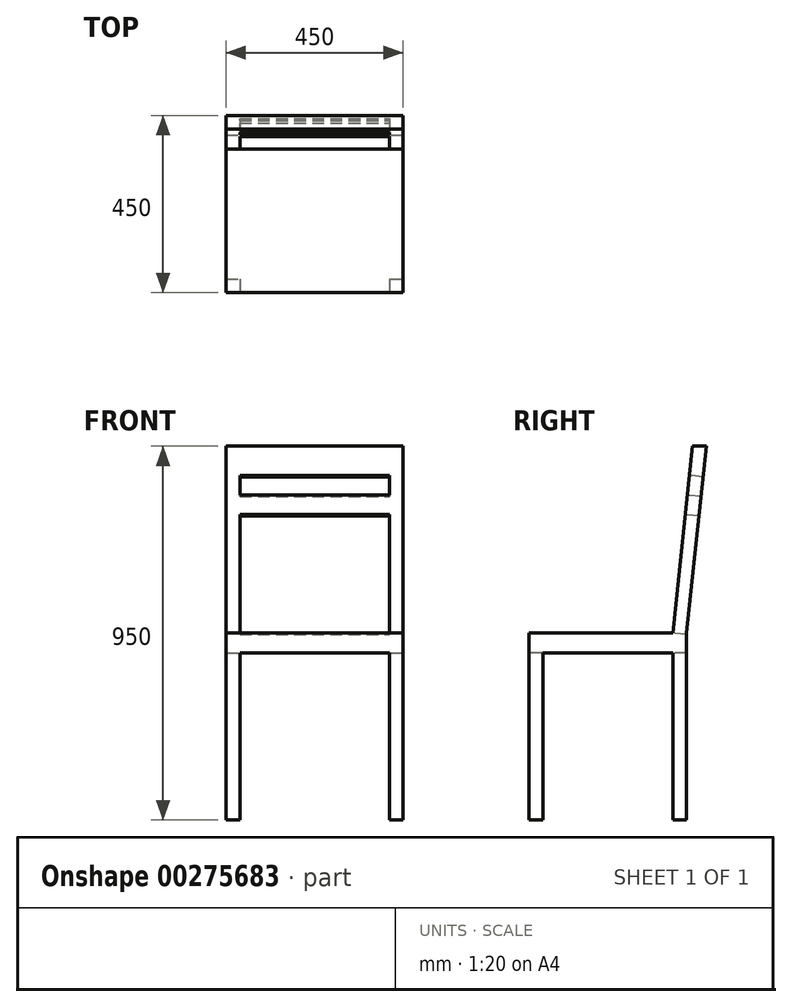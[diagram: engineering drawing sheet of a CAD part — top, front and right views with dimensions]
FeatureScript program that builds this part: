
annotation { "Feature Type Name" : "Feature", "Feature Type Description" : "" }
export const myFeature = defineFeature(function(context is Context, id is Id, definition is map)
    precondition{}
    {
        {
            var Q0;
            Q0=qCreatedBy(makeId("Top.planeOp"),FACE);
            var sketch = newSketch(context, id + "F0", { "sketchPlane" : qUnion([Q0])});
            skLineSegment(sketch, "E0.bottom", {"start": v(225, 225) * mm, "end": v(-225, 225) * mm});
            skLineSegment(sketch, "E0.top", {"start": v(225, -225) * mm, "end": v(-225, -225) * mm});
            skLineSegment(sketch, "E0.left", {"start": v(225, 225) * mm, "end": v(225, -225) * mm});
            skLineSegment(sketch, "E0.right", {"start": v(-225, 225) * mm, "end": v(-225, -225) * mm});
            skPoint(sketch, "E0.middle", {"position": v(0, 0) * mm});
            skSolve(sketch);
        }
        {
            var Q0;
            Q0=qSketchRegion(id+"F0",true);
            extrude(context, id + "F1", {"entities" : qUnion([Q0]), "depth" : 950 * mm});
        }
        {
            var Q0;
            Q0=makeQuery(id+"F1.opExtrude","SWEPT_FACE",FACE,{"disambiguationData":[OSD([sQuery(id+"F0.wireOp",EDGE,"E0.left")])]});
            var sketch = newSketch(context, id + "F2", { "sketchPlane" : qUnion([Q0])});
            skLineSegment(sketch, "E1.bottom", {"start": v(225, 475) * mm, "end": v(-225, 475) * mm});
            skLineSegment(sketch, "E1.top", {"start": v(225, 475) * mm, "end": v(-225, 475) * mm});
            skLineSegment(sketch, "E1.left", {"start": v(225, 475) * mm, "end": v(225, 475) * mm});
            skLineSegment(sketch, "E1.right", {"start": v(-225, 475) * mm, "end": v(-225, 475) * mm});
            skLineSegment(sketch, "E2.bottom", {"start": v(-225, 425) * mm, "end": v(225, 425) * mm});
            skLineSegment(sketch, "E2.top", {"start": v(-225, 475) * mm, "end": v(225, 475) * mm});
            skLineSegment(sketch, "E2.left", {"start": v(-225, 425) * mm, "end": v(-225, 475) * mm});
            skLineSegment(sketch, "E2.right", {"start": v(225, 425) * mm, "end": v(225, 475) * mm});
            skLineSegment(sketch, "E3", {"start": v(225, 950) * mm, "end": v(175, 475) * mm});
            skLineSegment(sketch, "E4", {"start": v(190, 950) * mm, "end": v(140, 475) * mm});
            skLineSegment(sketch, "E5", {"start": v(140, 475) * mm, "end": v(140, 0) * mm});
            skLineSegment(sketch, "E6", {"start": v(175, 475) * mm, "end": v(175, 0) * mm});
            skLineSegment(sketch, "E7.bottom", {"start": v(-225, 425) * mm, "end": v(-190, 425) * mm});
            skLineSegment(sketch, "E7.top", {"start": v(-225, 0) * mm, "end": v(-190, 0) * mm});
            skLineSegment(sketch, "E7.left", {"start": v(-225, 425) * mm, "end": v(-225, 0) * mm});
            skLineSegment(sketch, "E7.right", {"start": v(-190, 425) * mm, "end": v(-190, 0) * mm});
            skSolve(sketch);
        }
        {
            var Q0;
            {var subQ0=sQuery(id+"F2.wireOp",EDGE,"E2.right");Q0=makeQuery(id+"F2.imprint","IMPRINT",FACE,{"disambiguationData":[TD([[makeQuery(id+"F2.imprint","IMPRINT",EDGE,{"derivedFrom":subQ0}),-1.0]])]});}
            var Q1;
            {var subQ4=sQuery(id+"F2.wireOp",EDGE,"E4");Q1=makeQuery(id+"F2.imprint","IMPRINT",FACE,{"disambiguationData":[TD([[makeQuery(id+"F2.imprint","IMPRINT",EDGE,{"derivedFrom":subQ4}),-1.0]])]});}
            var Q2;
            {var subQ0=sQuery(id+"F2.wireOp",EDGE,"E7.right");Q2=makeQuery(id+"F2.imprint","IMPRINT",FACE,{"disambiguationData":[TD([[makeQuery(id+"F2.imprint","IMPRINT",EDGE,{"derivedFrom":subQ0}),1.0]])]});}
            var Q3;
            {var subQ1=sQuery(id+"F0.wireOp",EDGE,"E0.left");var subQ4=sQuery(id+"F2.wireOp",EDGE,"E6");var subQ6=makeQuery(id+"F1.opExtrude","CAP_EDGE",EDGE,{"disambiguationData":[OSD([subQ1])],"isStart":true});var subQ7=makeQuery(id+"F2.imprint","INTERSECT",VERTEX,{"derivedFrom":[subQ6,subQ4]});Q3=makeQuery(id+"F2.imprint","IMPRINT",FACE,{"disambiguationData":[TD([[makeQuery(id+"F2.imprint","IMPRINT",EDGE,{"disambiguationData":[TD([[subQ7,1.0]])],"derivedFrom":subQ4}),1.0]])]});}
            var Q4;
            {var subQ4=sQuery(id+"F2.wireOp",EDGE,"E3");Q4=makeQuery(id+"F2.imprint","IMPRINT",FACE,{"disambiguationData":[TD([[makeQuery(id+"F2.imprint","IMPRINT",EDGE,{"derivedFrom":subQ4}),1.0]])]});}
            extrude(context, id + "F3", {"entities" : qUnion([Q0, Q1, Q2, Q3, Q4]), "operationType" : NewBodyOperationType.REMOVE, "endBound" : BoundingType.THROUGH_ALL, "oppositeDirection" : true, "depth" : 25 * mm});
        }
        {
            var Q0;
            Q0=makeQuery(id+"F1.opExtrude","SWEPT_FACE",FACE,{"disambiguationData":[OSD([sQuery(id+"F0.wireOp",EDGE,"E0.top")])]});
            var sketch = newSketch(context, id + "F4", { "sketchPlane" : qUnion([Q0])});
            skLineSegment(sketch, "E8", {"start": v(-190, 425) * mm, "end": v(-190, 0) * mm});
            skLineSegment(sketch, "E9", {"start": v(-190, 425) * mm, "end": v(190, 425) * mm});
            skLineSegment(sketch, "E10", {"start": v(190, 425) * mm, "end": v(190, 0) * mm});
            skSolve(sketch);
        }
        {
            var Q0;
            Q0 = qSketchRegion(id + "F4", true);
            var Q1;
            {var subQ0=sQuery(id+"F4.wireOp",EDGE,"E8");Q1=makeQuery(id+"F4.imprint","IMPRINT",FACE,{"disambiguationData":[TD([[makeQuery(id+"F4.imprint","IMPRINT",EDGE,{"derivedFrom":subQ0}),1.0]])]});}
            extrude(context, id + "F5", {"entities" : qUnion([Q0, Q1]), "operationType" : NewBodyOperationType.REMOVE, "endBound" : BoundingType.THROUGH_ALL, "oppositeDirection" : true, "depth" : 25 * mm});
        }
        {
            var Q0;
            Q0=makeQuery(id+"F3.boolean.opBoolean","COPY",FACE,{"derivedFrom":makeQuery(id+"F3.opExtrude","SWEPT_FACE",FACE,{"disambiguationData":[OSD([sQuery(id+"F2.wireOp",EDGE,"E4")])]})});
            var sketch = newSketch(context, id + "F6", { "sketchPlane" : qUnion([Q0])});
            skLineSegment(sketch, "E11", {"start": v(-190, 487.05) * mm, "end": v(-190, 889.67) * mm});
            skLineSegment(sketch, "E12", {"start": v(-190, 889.67) * mm, "end": v(190, 889.67) * mm});
            skLineSegment(sketch, "E13", {"start": v(190, 889.67) * mm, "end": v(190, 487.05) * mm});
            skLineSegment(sketch, "E14", {"start": v(-190, 839.67) * mm, "end": v(190, 839.67) * mm});
            skLineSegment(sketch, "E15", {"start": v(-190, 789.67) * mm, "end": v(190, 789.67) * mm});
            skSolve(sketch);
        }
        {
            var Q0;
            {var subQ0=sQuery(id+"F6.wireOp",EDGE,"E12");Q0=makeQuery(id+"F6.imprint","IMPRINT",FACE,{"disambiguationData":[TD([[makeQuery(id+"F6.imprint","IMPRINT",EDGE,{"derivedFrom":subQ0}),-1.0]])]});}
            var Q1;
            {var subQ3=sQuery(id+"F6.wireOp",EDGE,"E15");Q1=makeQuery(id+"F6.imprint","IMPRINT",FACE,{"disambiguationData":[TD([[makeQuery(id+"F6.imprint","IMPRINT",EDGE,{"derivedFrom":subQ3}),-1.0]])]});}
            extrude(context, id + "F7", {"entities" : qUnion([Q0, Q1]), "operationType" : NewBodyOperationType.REMOVE, "endBound" : BoundingType.THROUGH_ALL, "oppositeDirection" : true, "depth" : 25 * mm});
        }
    });
